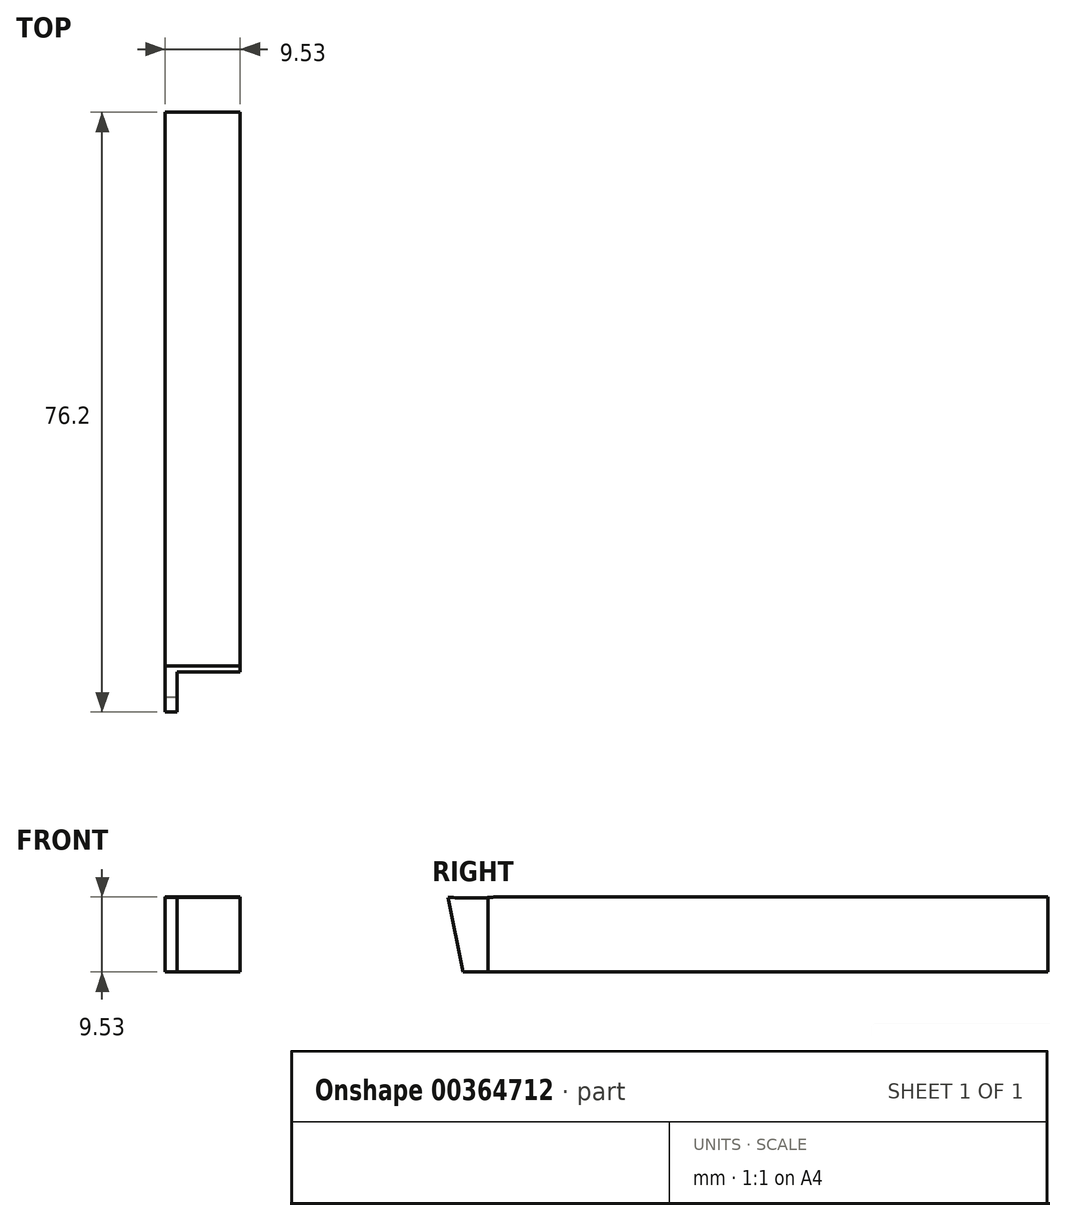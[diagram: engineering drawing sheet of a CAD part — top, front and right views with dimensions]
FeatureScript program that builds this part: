
annotation { "Feature Type Name" : "Feature", "Feature Type Description" : "" }
export const myFeature = defineFeature(function(context is Context, id is Id, definition is map)
    precondition{}
    {
        {
            var Q0;
            Q0=qCreatedBy(makeId("Top.planeOp"),FACE);
            var sketch = newSketch(context, id + "F0", { "sketchPlane" : qUnion([Q0])});
            skLineSegment(sketch, "E0.bottom", {"start": v(0, 0) * mm, "end": v(9.53, 0) * mm});
            skLineSegment(sketch, "E0.top", {"start": v(0, 76.2) * mm, "end": v(9.52, 76.2) * mm});
            skLineSegment(sketch, "E0.left", {"start": v(0, 0) * mm, "end": v(0, 76.2) * mm});
            skLineSegment(sketch, "E0.right", {"start": v(9.53, 0) * mm, "end": v(9.53, 76.2) * mm});
            skSolve(sketch);
        }
        {
            var Q0;
            Q0 = qSketchRegion(id + "F0", true);
            extrude(context, id + "F1", {"entities" : qUnion([Q0]), "depth" : 9.52 * mm});
        }
        {
            var Q0;
            Q0=makeQuery(id+"F1.opExtrude","CAP_FACE",FACE,{"disambiguationData":[OSD([sQuery(id+"F0.wireOp",EDGE,"E0.bottom"),sQuery(id+"F0.wireOp",EDGE,"E0.top"),sQuery(id+"F0.wireOp",EDGE,"E0.left"),sQuery(id+"F0.wireOp",EDGE,"E0.right")])],"isStart":false});
            var sketch = newSketch(context, id + "F2", { "sketchPlane" : qUnion([Q0])});
            skLineSegment(sketch, "E1", {"start": v(1.52, -3.86) * mm, "end": v(1.52, 5.08) * mm});
            skLineSegment(sketch, "E2", {"start": v(1.52, 5.08) * mm, "end": v(13.94, 5.08) * mm});
            skLineSegment(sketch, "E3", {"start": v(13.94, 5.08) * mm, "end": v(13.94, -4.22) * mm});
            skLineSegment(sketch, "E4", {"start": v(13.94, -4.22) * mm, "end": v(1.52, -3.86) * mm});
            skSolve(sketch);
        }
        {
            var Q0;
            {var subQ0=sQuery(id+"F2.wireOp",EDGE,"E3");Q0=makeQuery(id+"F2.imprint","IMPRINT",FACE,{"disambiguationData":[TD([[makeQuery(id+"F2.imprint","IMPRINT",EDGE,{"derivedFrom":subQ0}),-1.0]])]});}
            var Q1;
            {var subQ0=sQuery(id+"F2.wireOp",EDGE,"E2");var subQ1=sQuery(id+"F2.wireOp",EDGE,"E1");var subQ2=makeQuery(id+"F2.imprint","INTERSECT",VERTEX,{"derivedFrom":[subQ1,subQ0]});Q1=makeQuery(id+"F2.imprint","IMPRINT",FACE,{"disambiguationData":[TD([[makeQuery(id+"F2.imprint","IMPRINT",EDGE,{"disambiguationData":[TD([[subQ2,1.0]])],"derivedFrom":subQ1}),-1.0]])]});}
            extrude(context, id + "F3", {"entities" : qUnion([Q0, Q1]), "operationType" : NewBodyOperationType.REMOVE, "oppositeDirection" : true, "depth" : 25.4 * mm});
        }
        {
            var Q0;
            Q0=makeQuery(id+"F1.opExtrude","SWEPT_FACE",FACE,{"disambiguationData":[OSD([sQuery(id+"F0.wireOp",EDGE,"E0.right")])]});
            var sketch = newSketch(context, id + "F4", { "sketchPlane" : qUnion([Q0])});
            skCircle(sketch, "E5", {"center": v(2.74, 48.62) * mm, "radius": 39.22 * mm});
            skSolve(sketch);
        }
        {
            var Q0;
            Q0 = qSketchRegion(id + "F4", true);
            extrude(context, id + "F5", {"entities" : qUnion([Q0]), "operationType" : NewBodyOperationType.REMOVE, "oppositeDirection" : true, "depth" : 25.4 * mm});
        }
        {
            var Q0;
            Q0=makeQuery(id+"F1.opExtrude","SWEPT_FACE",FACE,{"disambiguationData":[OSD([sQuery(id+"F0.wireOp",EDGE,"E0.right")])]});
            var sketch = newSketch(context, id + "F6", { "sketchPlane" : qUnion([Q0])});
            skLineSegment(sketch, "E6", {"start": v(0, 9.5) * mm, "end": v(2.3, -2.03) * mm});
            skLineSegment(sketch, "E7.0", {"start": v(0, 9.5) * mm, "end": v(0, 0) * mm});
            skLineSegment(sketch, "E8", {"start": v(0, 0) * mm, "end": v(2.3, -2.03) * mm});
            skSolve(sketch);
        }
        {
            var Q0;
            Q0 = qSketchRegion(id + "F6", true);
            extrude(context, id + "F7", {"entities" : qUnion([Q0]), "operationType" : NewBodyOperationType.REMOVE, "oppositeDirection" : true, "depth" : 25.4 * mm});
        }
    });
